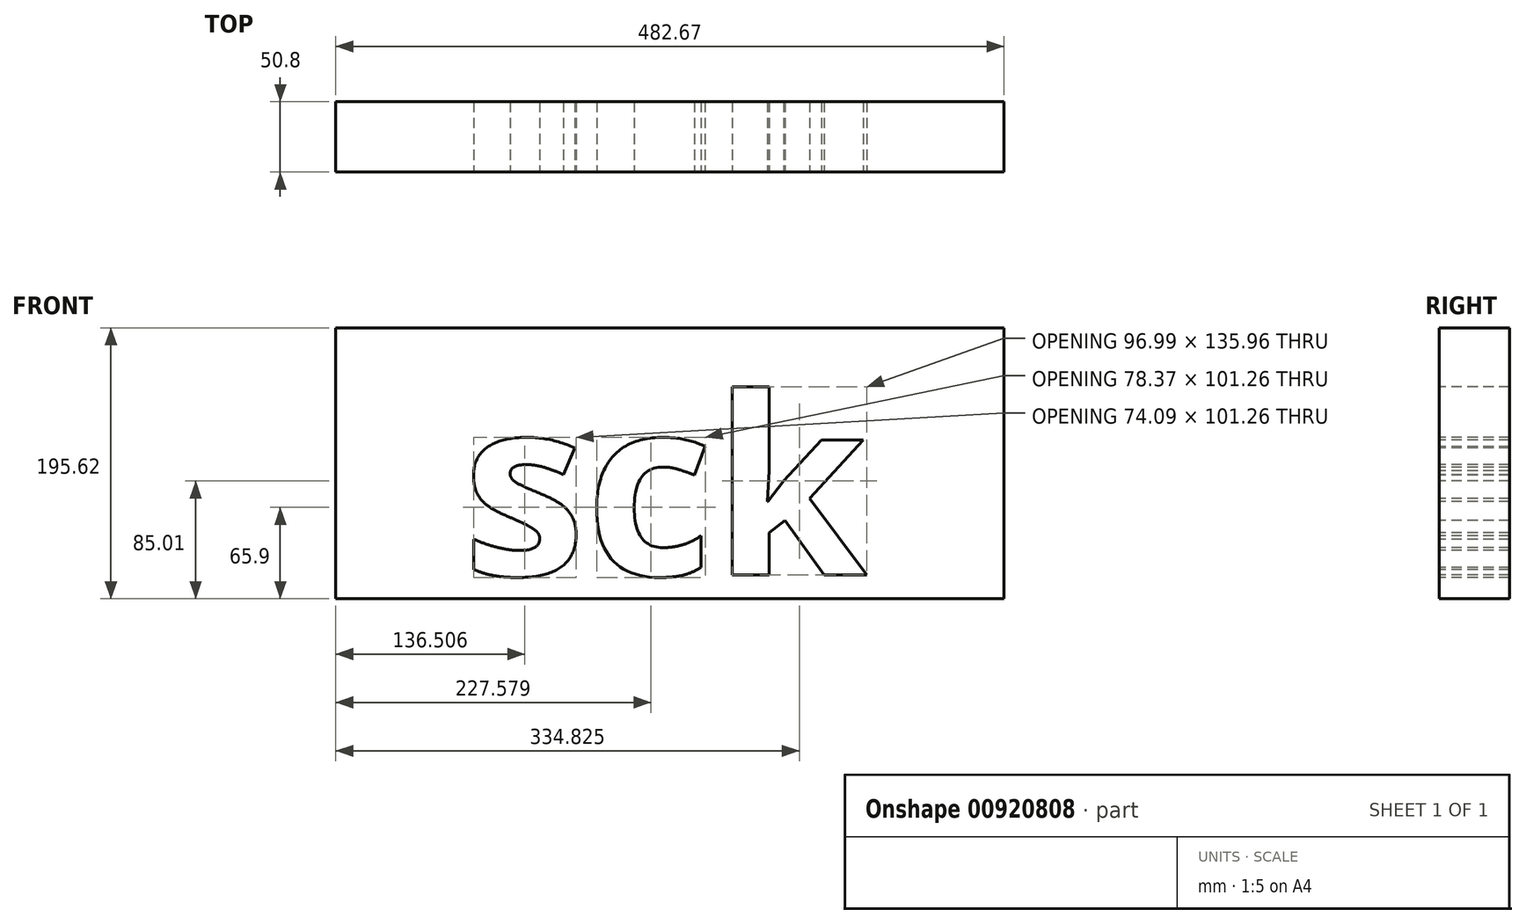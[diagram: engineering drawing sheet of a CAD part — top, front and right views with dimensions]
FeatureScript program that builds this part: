
annotation { "Feature Type Name" : "Feature", "Feature Type Description" : "" }
export const myFeature = defineFeature(function(context is Context, id is Id, definition is map)
    precondition{}
    {
        {
            var Q0;
            Q0=qCreatedBy(makeId("Front.planeOp"),FACE);
            var sketch = newSketch(context, id + "F0", { "sketchPlane" : qUnion([Q0])});
            skLineSegment(sketch, "E0.bottom", {"start": v(-235.62, 101.46) * mm, "end": v(247.05, 101.46) * mm});
            skLineSegment(sketch, "E0.top", {"start": v(-235.62, -94.16) * mm, "end": v(247.05, -94.16) * mm});
            skLineSegment(sketch, "E0.left", {"start": v(-235.62, 101.46) * mm, "end": v(-235.62, -94.16) * mm});
            skLineSegment(sketch, "E0.right", {"start": v(247.05, 101.46) * mm, "end": v(247.05, -94.16) * mm});
            skSolve(sketch);
        }
        {
            var Q0;
            Q0=makeQuery(id+"F0.imprint","IMPRINT",FACE,{"disambiguationData":[TD([[makeQuery(id+"F0.imprint","IMPRINT",EDGE,{"derivedFrom":sQuery(id+"F0.wireOp",EDGE,"E0.bottom")}),-1.0]])]});
            extrude(context, id + "F1", {"entities" : qUnion([Q0]), "depth" : 25.4 * mm, "offsetDistance" : 25.4 * mm, "hasSecondDirection" : true, "secondDirectionOppositeDirection" : true, "secondDirectionDepth" : 25.4 * mm});
        }
        {
            var Q0;
            Q0=qCreatedBy(makeId("Front.planeOp"),FACE);
            var sketch = newSketch(context, id + "F2", { "sketchPlane" : qUnion([Q0])});
            skText(sketch, "E1", { "text": "sck", "fontName": "OpenSans-Bold.ttf"});
            const initialGuessF2  = {"E1": [-0.14421, -0.07713, 1, 0, 0.12883]};
            skSetInitialGuess(sketch, initialGuessF2);
            skSolve(sketch);
        }
        {
            var Q0;
            Q0 = qSketchRegion(id + "F2", true);
            extrude(context, id + "F3", {"entities" : qUnion([Q0]), "operationType" : NewBodyOperationType.REMOVE, "oppositeDirection" : true, "depth" : 25.4 * mm, "offsetDistance" : 25.4 * mm, "hasSecondDirection" : true, "secondDirectionOppositeDirection" : false, "secondDirectionDepth" : 25.4 * mm});
        }
    });
